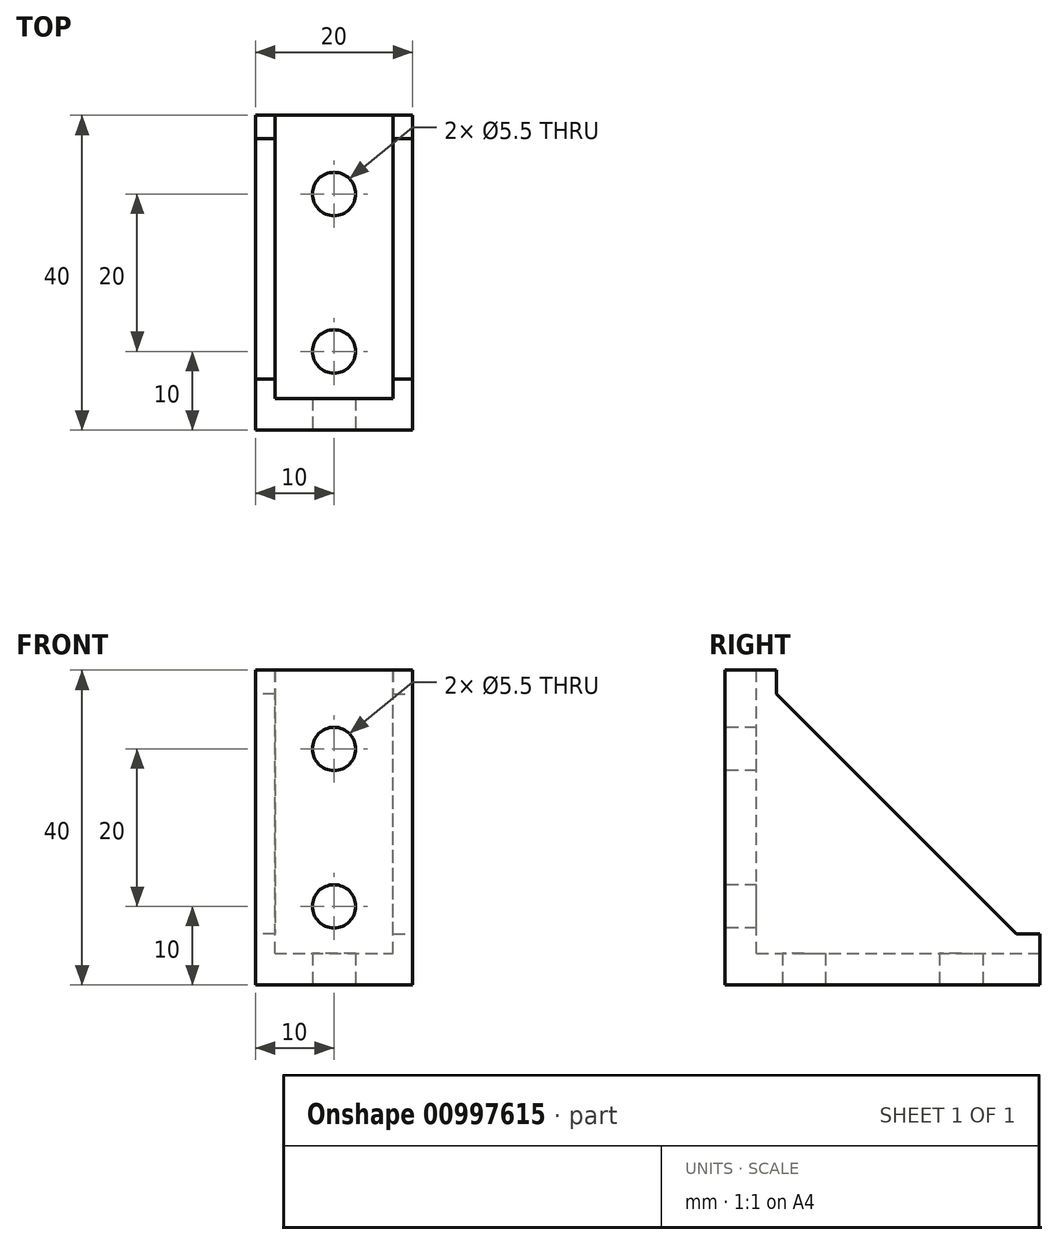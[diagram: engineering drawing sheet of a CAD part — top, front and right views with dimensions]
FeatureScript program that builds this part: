
annotation { "Feature Type Name" : "Feature", "Feature Type Description" : "" }
export const myFeature = defineFeature(function(context is Context, id is Id, definition is map)
    precondition{}
    {
        {
            var Q0;
            Q0=qCreatedBy(makeId("Top.planeOp"),FACE);
            var sketch = newSketch(context, id + "F0", { "sketchPlane" : qUnion([Q0])});
            skLineSegment(sketch, "E0.bottom", {"start": v(0, 0) * mm, "end": v(-20, 0) * mm});
            skLineSegment(sketch, "E0.top", {"start": v(0, 40) * mm, "end": v(-20, 40) * mm});
            skLineSegment(sketch, "E0.left", {"start": v(0, 0) * mm, "end": v(0, 40) * mm});
            skLineSegment(sketch, "E0.right", {"start": v(-20, 0) * mm, "end": v(-20, 40) * mm});
            skSolve(sketch);
        }
        {
            var Q0;
            Q0=makeQuery(id+"F0.imprint","IMPRINT",FACE,{"disambiguationData":[TD([[makeQuery(id+"F0.imprint","IMPRINT",EDGE,{"derivedFrom":sQuery(id+"F0.wireOp",EDGE,"E0.bottom")}),-1.0]])]});
            extrude(context, id + "F1", {"entities" : qUnion([Q0]), "depth" : 4 * mm, "offsetDistance" : 25 * mm});
        }
        {
            var Q0;
            Q0=qCreatedBy(makeId("Front.planeOp"),FACE);
            var sketch = newSketch(context, id + "F2", { "sketchPlane" : qUnion([Q0])});
            skLineSegment(sketch, "E1.bottom", {"start": v(0, 0) * mm, "end": v(-20, 0) * mm});
            skLineSegment(sketch, "E1.top", {"start": v(0, 40) * mm, "end": v(-20, 40) * mm});
            skLineSegment(sketch, "E1.left", {"start": v(0, 0) * mm, "end": v(0, 40) * mm});
            skLineSegment(sketch, "E1.right", {"start": v(-20, 0) * mm, "end": v(-20, 40) * mm});
            skSolve(sketch);
        }
        {
            var Q0;
            Q0=makeQuery(id+"F2.imprint","IMPRINT",FACE,{"disambiguationData":[TD([[makeQuery(id+"F2.imprint","IMPRINT",EDGE,{"derivedFrom":sQuery(id+"F2.wireOp",EDGE,"E1.bottom")}),-1.0]])]});
            extrude(context, id + "F3", {"entities" : qUnion([Q0]), "operationType" : NewBodyOperationType.ADD, "oppositeDirection" : true, "depth" : 4 * mm, "offsetDistance" : 25 * mm});
        }
        {
            var Q0;
            Q0=makeQuery(id+"F3.boolean.opBoolean","MERGE",FACE,{"derivedFrom":[makeQuery(id+"F1.opExtrude","SWEPT_FACE",FACE,{"disambiguationData":[OSD([sQuery(id+"F0.wireOp",EDGE,"E0.bottom")])]}),makeQuery(id+"F3.opExtrude","CAP_FACE",FACE,{"disambiguationData":[OSD([sQuery(id+"F2.wireOp",EDGE,"E1.bottom"),sQuery(id+"F2.wireOp",EDGE,"E1.top"),sQuery(id+"F2.wireOp",EDGE,"E1.left"),sQuery(id+"F2.wireOp",EDGE,"E1.right")])],"isStart":true})]});
            var sketch = newSketch(context, id + "F4", { "sketchPlane" : qUnion([Q0])});
            skPoint(sketch, "E2", {"position": v(-10, 30) * mm});
            skPoint(sketch, "E2.positionSnap0", {"position": v(-10, 40) * mm});
            skPoint(sketch, "E3", {"position": v(-10, 10) * mm});
            skSolve(sketch);
        }
        {
            var Q0;
            Q0=makeQuery(id+"F3.boolean.opBoolean","MERGE",FACE,{"derivedFrom":[makeQuery(id+"F1.opExtrude","SWEPT_FACE",FACE,{"disambiguationData":[OSD([sQuery(id+"F0.wireOp",EDGE,"E0.left")])]}),makeQuery(id+"F3.opExtrude","SWEPT_FACE",FACE,{"disambiguationData":[OSD([sQuery(id+"F2.wireOp",EDGE,"E1.left")])]})]});
            var sketch = newSketch(context, id + "F5", { "sketchPlane" : qUnion([Q0])});
            skLineSegment(sketch, "E4", {"start": v(40, 4) * mm, "end": v(4, 4) * mm});
            skLineSegment(sketch, "E5", {"start": v(4, 4) * mm, "end": v(4, 40) * mm});
            skLineSegment(sketch, "E6", {"start": v(4, 40) * mm, "end": v(6.5, 40) * mm});
            skLineSegment(sketch, "E7", {"start": v(6.5, 40) * mm, "end": v(6.5, 37) * mm});
            skLineSegment(sketch, "E8", {"start": v(40, 4) * mm, "end": v(40, 6.5) * mm});
            skLineSegment(sketch, "E9", {"start": v(40, 6.5) * mm, "end": v(37, 6.5) * mm});
            skLineSegment(sketch, "E10", {"start": v(37, 6.5) * mm, "end": v(6.5, 37) * mm});
            skSolve(sketch);
        }
        {
            var Q0;
            Q0=makeQuery(id+"F3.boolean.opBoolean","MERGE",FACE,{"derivedFrom":[makeQuery(id+"F1.opExtrude","SWEPT_FACE",FACE,{"disambiguationData":[OSD([sQuery(id+"F0.wireOp",EDGE,"E0.right")])]}),makeQuery(id+"F3.opExtrude","SWEPT_FACE",FACE,{"disambiguationData":[OSD([sQuery(id+"F2.wireOp",EDGE,"E1.right")])]})]});
            var sketch = newSketch(context, id + "F6", { "sketchPlane" : qUnion([Q0])});
            skLineSegment(sketch, "E11", {"start": v(-4, 40) * mm, "end": v(-4, 4) * mm});
            skLineSegment(sketch, "E12", {"start": v(-4, 4) * mm, "end": v(-40, 4) * mm});
            skLineSegment(sketch, "E13", {"start": v(-40, 4) * mm, "end": v(-40, 6.5) * mm});
            skLineSegment(sketch, "E14", {"start": v(-40, 6.5) * mm, "end": v(-37, 6.5) * mm});
            skLineSegment(sketch, "E15", {"start": v(-4, 40) * mm, "end": v(-6.5, 40) * mm});
            skLineSegment(sketch, "E16", {"start": v(-6.5, 40) * mm, "end": v(-6.5, 37) * mm});
            skLineSegment(sketch, "E17", {"start": v(-6.5, 37) * mm, "end": v(-37, 6.5) * mm});
            skSolve(sketch);
        }
        {
            var Q0;
            Q0=makeQuery(id+"F6.imprint","IMPRINT",FACE,{"disambiguationData":[TD([[makeQuery(id+"F6.imprint","IMPRINT",EDGE,{"derivedFrom":sQuery(id+"F6.wireOp",EDGE,"E11")}),1.0]])]});
            extrude(context, id + "F7", {"entities" : qUnion([Q0]), "operationType" : NewBodyOperationType.ADD, "oppositeDirection" : true, "depth" : 2.5 * mm, "offsetDistance" : 25 * mm});
        }
        {
            var Q0;
            Q0 = qSketchRegion(id + "F5", true);
            extrude(context, id + "F8", {"entities" : qUnion([Q0]), "operationType" : NewBodyOperationType.ADD, "oppositeDirection" : true, "depth" : 2.5 * mm, "offsetDistance" : 25 * mm});
        }
        {
            var Q0;
            Q0=sQuery(id+"F4.wireOp",VERTEX,"E2");
            var Q1;
            Q1=sQuery(id+"F4.wireOp",VERTEX,"E3");
            var Q2;
            Q2=makeQuery(id+"F1.opExtrude","SWEPT_BODY",BODY,{"disambiguationData":[OSD([sQuery(id+"F0.wireOp",EDGE,"E0.bottom"),sQuery(id+"F0.wireOp",EDGE,"E0.top"),sQuery(id+"F0.wireOp",EDGE,"E0.left"),sQuery(id+"F0.wireOp",EDGE,"E0.right")])]});
            hole(context, id + "F9", {"style" : HoleStyle.SIMPLE, "endStyle" : HoleEndStyle.THROUGH, "standardTappedOrClearance" : lookupTablePath({ "fit" : "Normal", "standard" : "ISO", "size" : "M5", "type" : "Clearance" }), "standardBlindInLast" : lookupTablePath({ "fit" : "Normal", "standard" : "ISO", "engagement" : "75%", "pitch" : "0.8 mm", "size" : "M5", "type" : "Clearance & tapped" }), "holeDiameter" : 5.5 * mm, "majorDiameter" : 5 * mm, "isTappedThrough" : true, "tappedDepth" : 9 * mm, "tapClearance" : 2, "locations" : qUnion([Q0, Q1]), "scope" : qUnion([Q2])});
        }
        {
            var Q0;
            Q0=makeQuery(id+"F1.opExtrude","CAP_FACE",FACE,{"disambiguationData":[OSD([sQuery(id+"F0.wireOp",EDGE,"E0.bottom"),sQuery(id+"F0.wireOp",EDGE,"E0.top"),sQuery(id+"F0.wireOp",EDGE,"E0.left"),sQuery(id+"F0.wireOp",EDGE,"E0.right")])],"isStart":true});
            var sketch = newSketch(context, id + "F10", { "sketchPlane" : qUnion([Q0])});
            skPoint(sketch, "E18", {"position": v(-10, -30) * mm});
            skPoint(sketch, "E18.positionSnap0", {"position": v(-10, -40) * mm});
            skPoint(sketch, "E19", {"position": v(-10, -10) * mm});
            skSolve(sketch);
        }
        {
            var Q0;
            Q0=sQuery(id+"F10.wireOp",VERTEX,"E18");
            var Q1;
            Q1=sQuery(id+"F10.wireOp",VERTEX,"E19");
            var Q2;
            Q2=makeQuery(id+"F1.opExtrude","SWEPT_BODY",BODY,{"disambiguationData":[OSD([sQuery(id+"F0.wireOp",EDGE,"E0.bottom"),sQuery(id+"F0.wireOp",EDGE,"E0.top"),sQuery(id+"F0.wireOp",EDGE,"E0.left"),sQuery(id+"F0.wireOp",EDGE,"E0.right")])]});
            hole(context, id + "F11", {"style" : HoleStyle.SIMPLE, "endStyle" : HoleEndStyle.THROUGH, "standardTappedOrClearance" : lookupTablePath({ "fit" : "Normal", "standard" : "ISO", "size" : "M5", "type" : "Clearance" }), "standardBlindInLast" : lookupTablePath({ "fit" : "Normal", "standard" : "ISO", "engagement" : "75%", "pitch" : "0.8 mm", "size" : "M5", "type" : "Clearance & tapped" }), "holeDiameter" : 5.5 * mm, "majorDiameter" : 5 * mm, "isTappedThrough" : true, "tappedDepth" : 9 * mm, "tapClearance" : 2, "locations" : qUnion([Q0, Q1]), "scope" : qUnion([Q2])});
        }
    });
